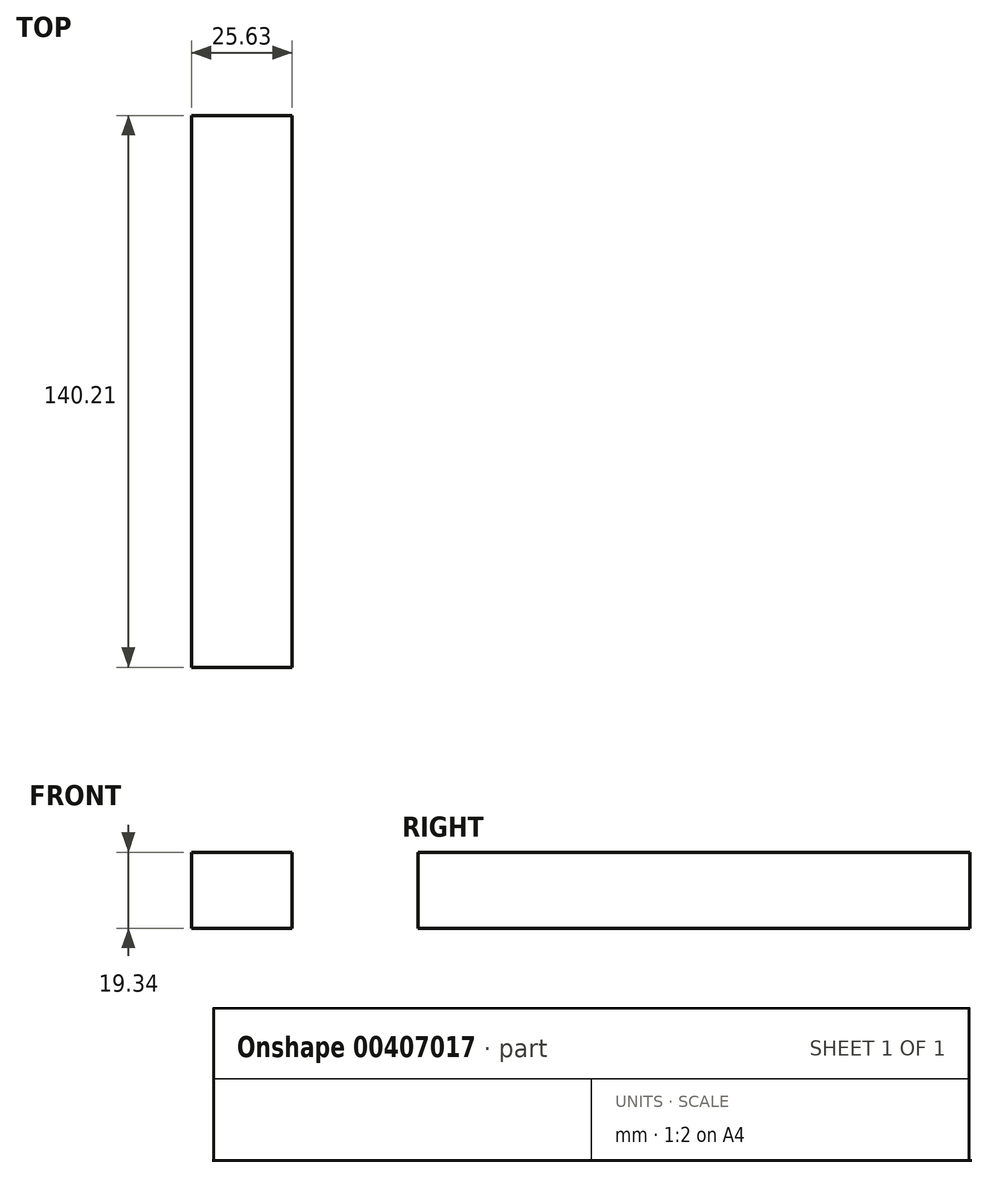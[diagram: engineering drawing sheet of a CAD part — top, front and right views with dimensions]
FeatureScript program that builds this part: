
annotation { "Feature Type Name" : "Feature", "Feature Type Description" : "" }
export const myFeature = defineFeature(function(context is Context, id is Id, definition is map)
    precondition{}
    {
        {
            var Q0;
            Q0=qCreatedBy(makeId("Front.planeOp"),FACE);
            var sketch = newSketch(context, id + "F0", { "sketchPlane" : qUnion([Q0])});
            skLineSegment(sketch, "E0.bottom", {"start": v(0, 0) * mm, "end": v(25.63, 0) * mm});
            skLineSegment(sketch, "E0.top", {"start": v(0, 19.34) * mm, "end": v(25.63, 19.34) * mm});
            skLineSegment(sketch, "E0.left", {"start": v(0, 0) * mm, "end": v(0, 19.34) * mm});
            skLineSegment(sketch, "E0.right", {"start": v(25.63, 0) * mm, "end": v(25.63, 19.34) * mm});
            skSolve(sketch);
        }
        {
            var Q0;
            Q0=makeQuery(id+"F0.imprint","IMPRINT",FACE,{"disambiguationData":[TD([[makeQuery(id+"F0.imprint","IMPRINT",EDGE,{"derivedFrom":sQuery(id+"F0.wireOp",EDGE,"E0.bottom")}),1.0]])]});
            extrude(context, id + "F1", {"entities" : qUnion([Q0]), "depth" : 140.2 * mm});
        }
    });
